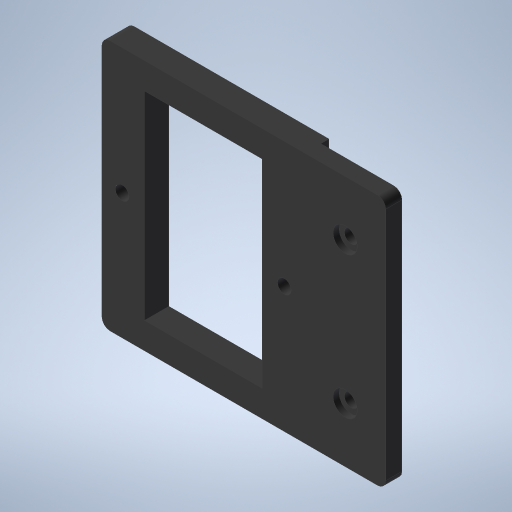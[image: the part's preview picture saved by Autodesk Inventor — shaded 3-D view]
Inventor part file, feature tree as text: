
AUTODESK INVENTOR PART (.ipt)
format: ipt  version: 2024.2 (Build 282272000, 272)  size: 262,144 bytes
history: native  units: in
note: dims shown in document units (in); Inventor stores cm internally (conversion verified against a paired STEP export)
features: extrude x3, sketch x3, fillet x1
ambient origin geometry x8: Origin, YZ Plane, XZ Plane, XY Plane, X Axis, Y Axis, Z Axis, Center Point
bodies: Solid1 (feature_tree)
feature tree (7):
  extrude  "Extrusion1"  Depth=0.1339in
  extrude  "Extrusion3"  Depth=1.1417in
  extrude  "Extrusion4"  Depth=0.0787in
  fillet  "Fillet1"  Radius=0.1969in
  sketch  "Sketch1"  dims[d0=0.1339in d1=0.1339in]
  sketch  "Sketch3"  dims[d2=1.5748in d3=1.1417in]
  sketch  "Sketch4"  dims[d4=1.9291in d5=0.1969in d6=0.1969in d7=2.4409in d8=0.2362in d9=0.0in d14=0.7874in d15=0.1339in d16=0.1339in d17=1.378in d18=0.1575in d19=0.0in d20=0.2362in d21=0.2362in d22=0.0591in d23=0.0in d24=0.0787in]
